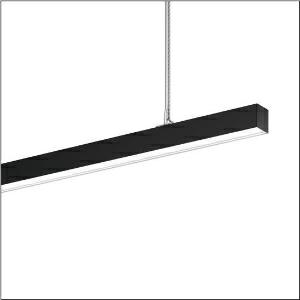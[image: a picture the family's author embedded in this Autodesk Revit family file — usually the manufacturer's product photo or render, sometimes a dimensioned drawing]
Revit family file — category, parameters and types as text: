
# Revit family: silica_r__21_51mx33db39bb_fd0d
name_source: partatom
category: Lighting Fixtures
units: mm (PartAtom-declared; Revit-internal decimal feet)

## family parameters
Cut with Voids When Loaded = No
Host = Face
Light Source = No
Part Type = Normal
Room Calculation Point = No
Round Connector Dimension = Use Diameter
Shared = No

## types (1)
- --- (1 x LED, 7390 lm, 51.6 W, 3000K)
    Apparent Load = 52 VA
    CIE Flux Codes = 78 96 99 55 100
    Color Rendering = 80
    Color Temperature = 3000K
    Default Elevation = 1800 mm
    Description = Silica® 21, office luminaire, primary optical cover: prismatic diffuser, of PMMA, CAT 2 (L<= 3000cd/m²), light emission: direct/indirect distribution, primary light characteristic: symmetric, installation type: suspended mounting, LED, rated luminous flux: 7.390lm, luminous efficacy: 143lm/W, light colour: 830, colour temperature: 3000K, with terminal, 3+2-pole, max. 2.5mm², mains connection: 220..240V, AC, 50/60Hz, rated input power: 51.6W, luminaire housing, of aluminium, jet black (RAL 9005), length: 1.504mm, width: 53mm, height: 53mm, protection rating (complete): IP20, insulation class (complete): insulation class I (protective earthing), certification: CE, permissible operating ambient temperature: 0..+35°C, standard: EN 50419, packaging unit: 1 piece
    Height = 53 mm
    Lamp = 1 x LED
    Lamp Light Flux = 7390 lm
    Lamp Power = 51.6 W
    Lamp count = 1
    Length = 1504 mm
    Luminous efficacy = 143 lm/W
    Manufacturer = Siteco
    ModVariant = No
    Model = 51MX33DB39BB
    Mounting Place = Ceiling
    Mounting Type = Pendant
    Number of Poles = 1
    OnlyDefault = Yes
    Power Factor = 1
    Product Name = Silica® 21
    Product group = office luminaire | ceiling pendant
    ProductGroupID = 902
    Protection Class = Protection class I
    Protection Degree = IP 20
    RLX_Detail_Level = 1
    RLX_Emergency_Light_Flux = 0 lm
    RLX_Emergency_Type = 0
    RLX_Emergency_Type_DB = No
    RlxData = <blob elided: 26241 chars, md5=c1700e0a>
    Socket = socket
    Standby Power = 0 W
    System Light Flux = 7390 lm
    System Power = 52 W
    Type Comments = factory setting: luminous flux: 100 % | dim-lin: 254 | 345 mA
    Type Image = l_1313646.jpg
    URL = http://relux.com
    VarID = @adj_066895
    Voltage = 0 V
    Weight = 0.00 kg
    Width = 53 mm

## geometry (parser evidence)
native form markers: Blend x4, Sweep x12
no freeform markers — native parametric forms only
